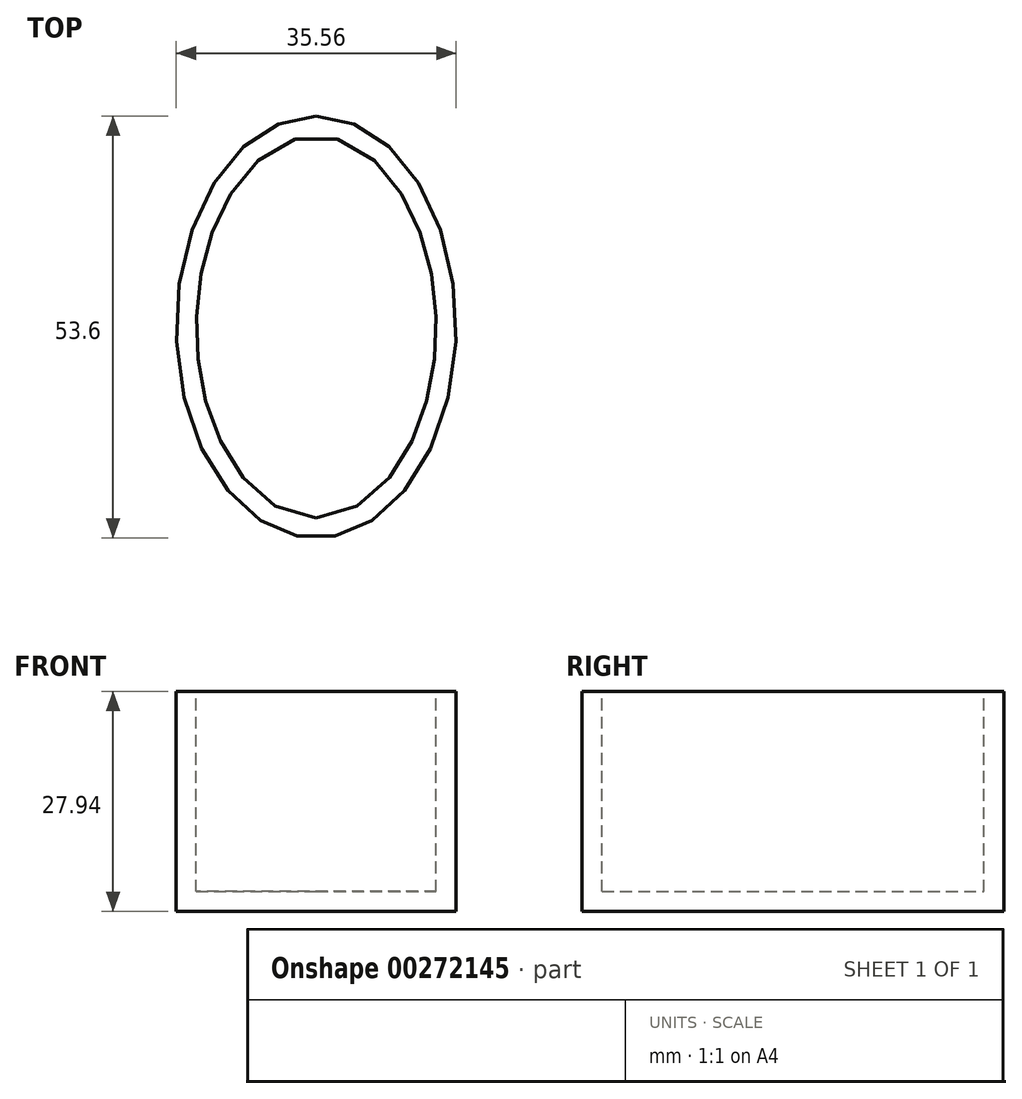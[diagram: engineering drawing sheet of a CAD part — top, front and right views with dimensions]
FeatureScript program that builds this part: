
annotation { "Feature Type Name" : "Feature", "Feature Type Description" : "" }
export const myFeature = defineFeature(function(context is Context, id is Id, definition is map)
    precondition{}
    {
        {
            var Q0;
            Q0=qCreatedBy(makeId("Top.planeOp"),FACE);
            var sketch = newSketch(context, id + "F0", { "sketchPlane" : qUnion([Q0])});
            skEllipse(sketch, "E0", {"center": v(0, 0) * mm, "majorRadius": 26.8 * mm, "minorRadius": 17.78 * mm, "majorAxis": v(0, 1)});
            skSolve(sketch);
        }
        {
            var Q0;
            Q0=makeQuery(id+"F0.imprint","IMPRINT",FACE,{"disambiguationData":[TD([[makeQuery(id+"F0.imprint","IMPRINT",EDGE,{"derivedFrom":sQuery(id+"F0.wireOp",EDGE,"E0")}),1.0]])]});
            extrude(context, id + "F1", {"entities" : qUnion([Q0]), "oppositeDirection" : true, "depth" : 27.94 * mm});
        }
        {
            var Q0;
            Q0=makeQuery(id+"F1.opExtrude","CAP_FACE",FACE,{"disambiguationData":[OSD([sQuery(id+"F0.wireOp",EDGE,"E0")])],"isStart":true});
            shell(context, id + "F2", {"entities" : qUnion([Q0]), "thickness" : 2.54 * mm});
        }
    });
